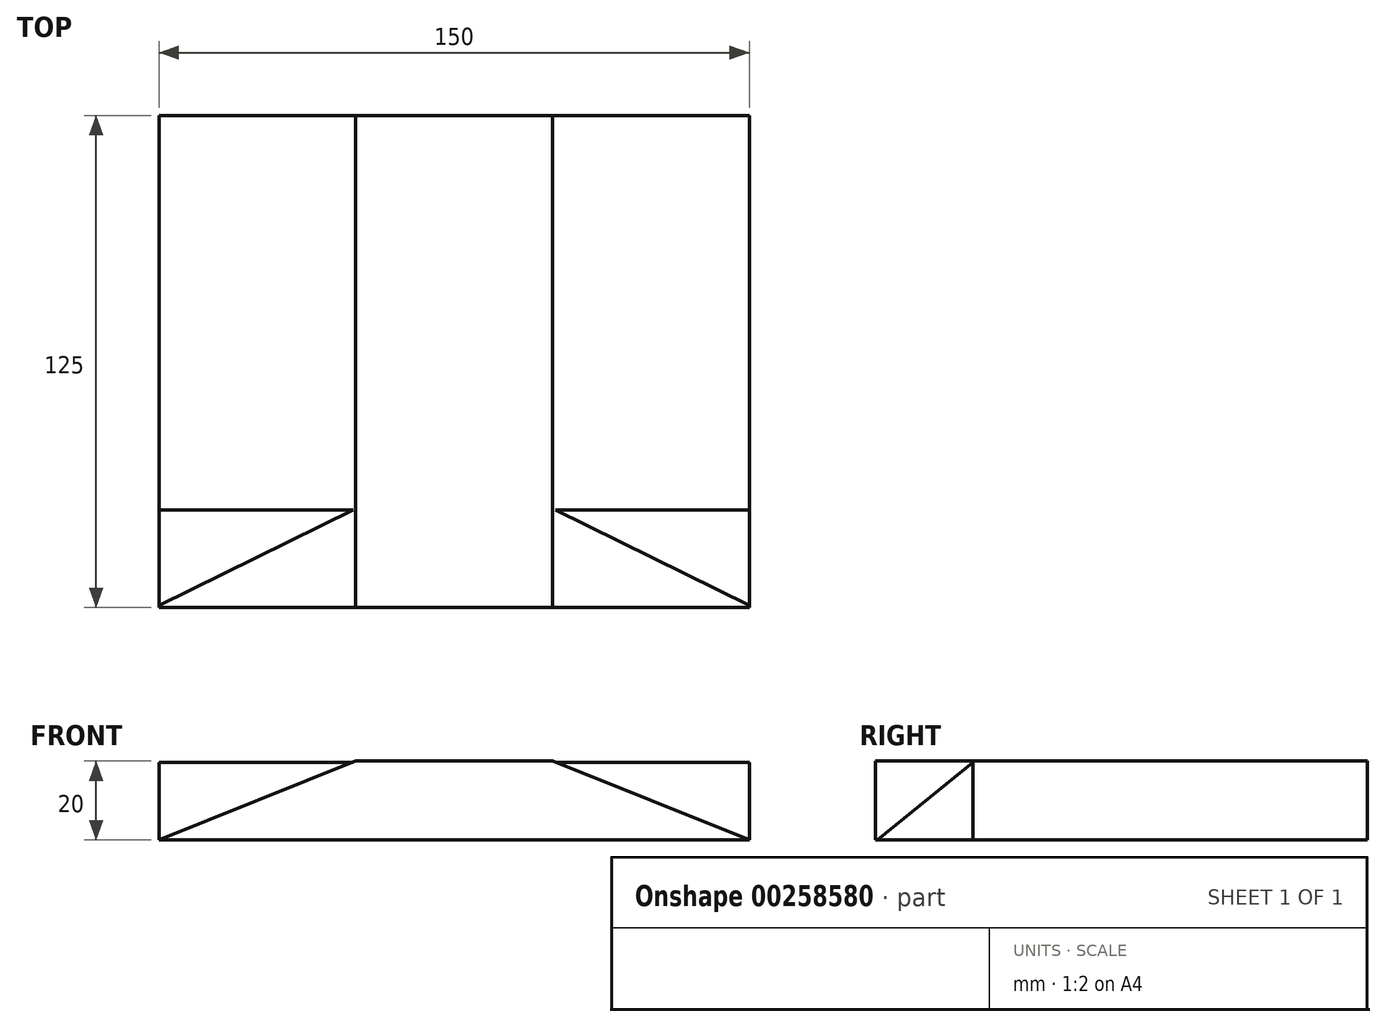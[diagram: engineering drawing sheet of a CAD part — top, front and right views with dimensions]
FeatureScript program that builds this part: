
annotation { "Feature Type Name" : "Feature", "Feature Type Description" : "" }
export const myFeature = defineFeature(function(context is Context, id is Id, definition is map)
    precondition{}
    {
        {
            var Q0;
            Q0=qCreatedBy(makeId("Front.planeOp"),FACE);
            var sketch = newSketch(context, id + "F0", { "sketchPlane" : qUnion([Q0])});
            skLineSegment(sketch, "E0", {"start": v(25, 20) * mm, "end": v(-25, 20) * mm});
            skPoint(sketch, "E1", {"position": v(0, 6.67) * mm});
            skLineSegment(sketch, "E2", {"start": v(25, 20) * mm, "end": v(75, 0) * mm});
            skLineSegment(sketch, "E3", {"start": v(75, 0) * mm, "end": v(-75, 0) * mm});
            skLineSegment(sketch, "E4", {"start": v(-75, 0) * mm, "end": v(-25, 20) * mm});
            skSolve(sketch);
        }
        {
            var Q0;
            Q0 = qSketchRegion(id + "F0", true);
            extrude(context, id + "F1", {"entities" : qUnion([Q0]), "depth" : 100 * mm});
        }
        {
            var Q0;
            Q0=makeQuery(id+"F1.opExtrude","CAP_FACE",FACE,{"disambiguationData":[OSD([sQuery(id+"F0.wireOp",EDGE,"E0"),sQuery(id+"F0.wireOp",EDGE,"E2"),sQuery(id+"F0.wireOp",EDGE,"E3"),sQuery(id+"F0.wireOp",EDGE,"E4")])],"isStart":false});
            extrude(context, id + "F2", {"entities" : qUnion([Q0]), "operationType" : NewBodyOperationType.ADD, "depth" : 25 * mm});
        }
        {
            var Q0;
            Q0=qCreatedBy(makeId("Right.planeOp"),FACE);
            var sketch = newSketch(context, id + "F3", { "sketchPlane" : qUnion([Q0])});
            skLineSegment(sketch, "E5", {"start": v(-100.16, 0) * mm, "end": v(-100.16, 19.7) * mm});
            skLineSegment(sketch, "E6", {"start": v(-100.16, 19.7) * mm, "end": v(-124.44, 0) * mm});
            skLineSegment(sketch, "E7", {"start": v(-124.44, 0) * mm, "end": v(-100.16, 0) * mm});
            skSolve(sketch);
        }
        {
            var Q0;
            Q0 = qSketchRegion(id + "F3", true);
            extrude(context, id + "F4", {"entities" : qUnion([Q0]), "operationType" : NewBodyOperationType.ADD, "depth" : 75 * mm});
        }
        {
            var Q0;
            Q0 = qSketchRegion(id + "F3", true);
            extrude(context, id + "F5", {"entities" : qUnion([Q0]), "operationType" : NewBodyOperationType.ADD, "oppositeDirection" : true, "depth" : 75 * mm});
        }
    });
